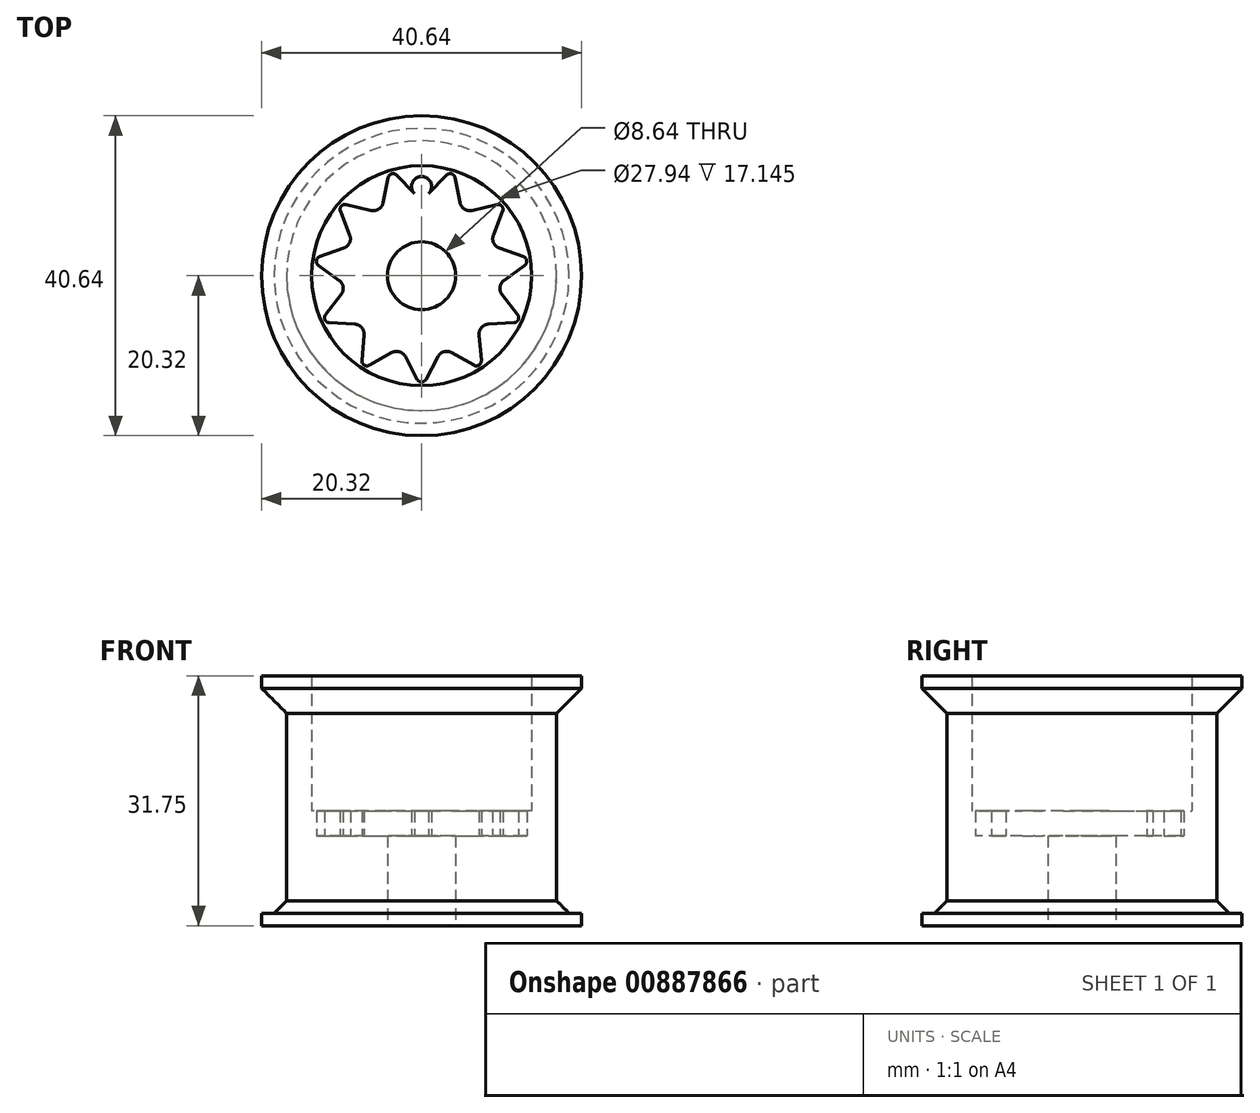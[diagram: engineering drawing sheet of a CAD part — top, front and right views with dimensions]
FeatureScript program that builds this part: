
annotation { "Feature Type Name" : "Feature", "Feature Type Description" : "" }
export const myFeature = defineFeature(function(context is Context, id is Id, definition is map)
    precondition{}
    {
        {
            var Q0;
            Q0=qCreatedBy(makeId("Top.planeOp"),FACE);
            var sketch = newSketch(context, id + "F0", { "sketchPlane" : qUnion([Q0])});
            skCircle(sketch, "E0", {"center": v(0, 0) * mm, "radius": 4.32 * mm});
            skCircle(sketch, "E1", {"center": v(0, 0) * mm, "radius": 15.88 * mm});
            skSolve(sketch);
        }
        {
            var Q0;
            Q0=makeQuery(id+"F0.imprint","IMPRINT",FACE,{"disambiguationData":[TD([[makeQuery(id+"F0.imprint","IMPRINT",EDGE,{"derivedFrom":sQuery(id+"F0.wireOp",EDGE,"E0")}),-1.0]])]});
            extrude(context, id + "F1", {"entities" : qUnion([Q0]), "depth" : 11.43 * mm, "offsetDistance" : 25.4 * mm});
        }
        {
            var Q0;
            Q0=qCreatedBy(makeId("Front.planeOp"),FACE);
            var sketch = newSketch(context, id + "F2", { "sketchPlane" : qUnion([Q0])});
            skLineSegment(sketch, "E2.bottom", {"start": v(0, 0) * mm, "end": v(-20.32, 0) * mm});
            skLineSegment(sketch, "E2.top", {"start": v(0, 0) * mm, "end": v(-20.32, 0) * mm});
            skLineSegment(sketch, "E2.left", {"start": v(0, 0) * mm, "end": v(0, 0) * mm});
            skLineSegment(sketch, "E2.right", {"start": v(-20.32, 0) * mm, "end": v(-20.32, 0) * mm});
            skLineSegment(sketch, "E3.top", {"start": v(-20.32, 1.59) * mm, "end": v(-20.32, 1.59) * mm});
            skLineSegment(sketch, "E3.left", {"start": v(-20.32, 0) * mm, "end": v(-20.32, 1.59) * mm});
            skLineSegment(sketch, "E3.right", {"start": v(-20.32, 0) * mm, "end": v(-20.32, 1.59) * mm});
            skLineSegment(sketch, "E4", {"start": v(-20.32, 1.59) * mm, "end": v(-17.15, 1.59) * mm});
            skLineSegment(sketch, "E5", {"start": v(-17.15, 1.59) * mm, "end": v(-17.15, 30.16) * mm});
            skLineSegment(sketch, "E6", {"start": v(-17.15, 30.16) * mm, "end": v(-20.32, 30.16) * mm});
            skLineSegment(sketch, "E7", {"start": v(-20.32, 30.16) * mm, "end": v(-20.32, 31.75) * mm});
            skLineSegment(sketch, "E8", {"start": v(-20.32, 31.75) * mm, "end": v(-13.97, 31.75) * mm});
            skLineSegment(sketch, "E9", {"start": v(0, 0) * mm, "end": v(-10.16, 0) * mm});
            skLineSegment(sketch, "E10", {"start": v(-10.16, 0) * mm, "end": v(-10.16, 1.59) * mm});
            skLineSegment(sketch, "E11", {"start": v(-10.16, 1.59) * mm, "end": v(-13.97, 1.59) * mm});
            skLineSegment(sketch, "E12", {"start": v(-13.97, 31.75) * mm, "end": v(-13.97, 1.59) * mm});
            skLineSegment(sketch, "E13", {"start": v(-20.32, 30.16) * mm, "end": v(-17.15, 26.99) * mm});
            skLineSegment(sketch, "E14", {"start": v(0, 0) * mm, "end": v(0, 23.16) * mm});
            skSolve(sketch);
        }
        {
            var Q0;
            {var subQ5=sQuery(id+"F2.wireOp",EDGE,"E3.left");Q0=makeQuery(id+"F2.imprint","IMPRINT",FACE,{"disambiguationData":[TD([[makeQuery(id+"F2.imprint","IMPRINT",EDGE,{"derivedFrom":subQ5}),-1.0]])]});}
            var Q1;
            {var subQ0=sQuery(id+"F2.wireOp",EDGE,"E6");Q1=makeQuery(id+"F2.imprint","IMPRINT",FACE,{"disambiguationData":[TD([[makeQuery(id+"F2.imprint","IMPRINT",EDGE,{"derivedFrom":subQ0}),1.0]])]});}
            var Q2;
            Q2=sQuery(id+"F2.wireOp",EDGE,"E14");
            revolve(context, id + "F3", {"operationType" : NewBodyOperationType.ADD, "surfaceOperationType" : NewSurfaceOperationType.NEW, "entities" : qUnion([Q0, Q1]), "axis" : qUnion([Q2]), "revolveType" : RevolveType.FULL});
        }
        {
            var Q0;
            Q0=makeQuery(id+"F1.opExtrude","CAP_FACE",FACE,{"disambiguationData":[OSD([sQuery(id+"F0.wireOp",EDGE,"E0"),sQuery(id+"F0.wireOp",EDGE,"E1")])],"isStart":false});
            var sketch = newSketch(context, id + "F4", { "sketchPlane" : qUnion([Q0])});
            skCircle(sketch, "E15", {"center": v(0, 0) * mm, "radius": 13.5 * mm});
            skLineSegment(sketch, "E16", {"start": v(0, 13.5) * mm, "end": v(0, 10.06) * mm});
            skCircle(sketch, "E17", {"center": v(0, 11.33) * mm, "radius": 1.27 * mm});
            skCircle(sketch, "E18.1.0", {"center": v(-6.13, 9.54) * mm, "radius": 1.27 * mm});
            skCircle(sketch, "E18.2.0", {"center": v(-10.31, 4.7) * mm, "radius": 1.27 * mm});
            skCircle(sketch, "E18.3.0", {"center": v(-11.22, -1.61) * mm, "radius": 1.27 * mm});
            skCircle(sketch, "E18.4.0", {"center": v(-8.57, -7.42) * mm, "radius": 1.27 * mm});
            skCircle(sketch, "E18.5.0", {"center": v(-3.2, -10.88) * mm, "radius": 1.27 * mm});
            skCircle(sketch, "E18.6.0", {"center": v(3.2, -10.88) * mm, "radius": 1.27 * mm});
            skCircle(sketch, "E18.7.0", {"center": v(8.57, -7.42) * mm, "radius": 1.27 * mm});
            skCircle(sketch, "E18.8.0", {"center": v(11.22, -1.61) * mm, "radius": 1.27 * mm});
            skCircle(sketch, "E18.9.0", {"center": v(10.31, 4.7) * mm, "radius": 1.27 * mm});
            skCircle(sketch, "E18.10.0", {"center": v(6.13, 9.54) * mm, "radius": 1.27 * mm});
            skLineSegment(sketch, "E19", {"start": v(0, 0) * mm, "end": v(3.8, 12.95) * mm});
            skCircle(sketch, "E20", {"center": v(3.62, 12.34) * mm, "radius": 0.64 * mm});
            skCircle(sketch, "E21.1.0", {"center": v(-3.62, 12.34) * mm, "radius": 0.64 * mm});
            skCircle(sketch, "E21.2.0", {"center": v(-9.72, 8.42) * mm, "radius": 0.64 * mm});
            skCircle(sketch, "E22.1.3.0", {"center": v(-12.73, 1.83) * mm, "radius": 0.64 * mm});
            skCircle(sketch, "E22.1.4.0", {"center": v(-11.7, -5.34) * mm, "radius": 0.64 * mm});
            skCircle(sketch, "E22.1.5.0", {"center": v(-6.95, -10.82) * mm, "radius": 0.64 * mm});
            skCircle(sketch, "E22.1.6.0", {"center": v(0, -12.86) * mm, "radius": 0.64 * mm});
            skCircle(sketch, "E22.1.7.0", {"center": v(6.95, -10.82) * mm, "radius": 0.64 * mm});
            skCircle(sketch, "E22.1.8.0", {"center": v(11.7, -5.34) * mm, "radius": 0.64 * mm});
            skCircle(sketch, "E22.1.9.0", {"center": v(12.73, 1.83) * mm, "radius": 0.64 * mm});
            skCircle(sketch, "E22.1.10.0", {"center": v(9.72, 8.42) * mm, "radius": 0.64 * mm});
            skLineSegment(sketch, "E23", {"start": v(-9.13, 5.17) * mm, "end": v(-10.3, 8.19) * mm});
            skLineSegment(sketch, "E24", {"start": v(-9.89, 3.51) * mm, "end": v(-12.94, 2.43) * mm});
            skLineSegment(sketch, "E25", {"start": v(-9.57, 9.04) * mm, "end": v(-6.42, 8.3) * mm});
            skLineSegment(sketch, "E26", {"start": v(-13.1, 1.32) * mm, "end": v(-10.47, -0.58) * mm});
            skLineSegment(sketch, "E27", {"start": v(-10.22, -2.4) * mm, "end": v(-12.2, -4.95) * mm});
            skLineSegment(sketch, "E28", {"start": v(-7.3, -7.53) * mm, "end": v(-7.58, -10.76) * mm});
            skLineSegment(sketch, "E29", {"start": v(-6.64, -11.37) * mm, "end": v(-3.82, -9.77) * mm});
            skLineSegment(sketch, "E30", {"start": v(-2.07, -10.29) * mm, "end": v(-0.56, -13.15) * mm});
            skLineSegment(sketch, "E31", {"start": v(0.56, -13.15) * mm, "end": v(2.07, -10.29) * mm});
            skLineSegment(sketch, "E32", {"start": v(3.82, -9.77) * mm, "end": v(6.64, -11.37) * mm});
            skLineSegment(sketch, "E33", {"start": v(7.58, -10.76) * mm, "end": v(7.3, -7.53) * mm});
            skLineSegment(sketch, "E34", {"start": v(8.5, -6.15) * mm, "end": v(11.73, -5.98) * mm});
            skLineSegment(sketch, "E35", {"start": v(-4.88, 9.29) * mm, "end": v(-4.25, 12.46) * mm});
            skLineSegment(sketch, "E36", {"start": v(-3.17, 12.78) * mm, "end": v(-0.91, 10.45) * mm});
            skLineSegment(sketch, "E37", {"start": v(0.91, 10.45) * mm, "end": v(3.17, 12.78) * mm});
            skLineSegment(sketch, "E38", {"start": v(10.3, 8.19) * mm, "end": v(9.13, 5.17) * mm});
            skLineSegment(sketch, "E39", {"start": v(9.89, 3.51) * mm, "end": v(12.94, 2.43) * mm});
            skLineSegment(sketch, "E40", {"start": v(13.1, 1.32) * mm, "end": v(10.47, -0.58) * mm});
            skLineSegment(sketch, "E41", {"start": v(10.22, -2.4) * mm, "end": v(12.2, -4.95) * mm});
            skLineSegment(sketch, "E42", {"start": v(4.25, 12.46) * mm, "end": v(4.88, 9.29) * mm});
            skLineSegment(sketch, "E43", {"start": v(6.42, 8.3) * mm, "end": v(9.57, 9.04) * mm});
            skLineSegment(sketch, "E44", {"start": v(-11.73, -5.98) * mm, "end": v(-8.5, -6.15) * mm});
            skCircle(sketch, "E45", {"center": v(0, 0) * mm, "radius": 15.88 * mm});
            skSolve(sketch);
        }
        {
            var Q0;
            Q0=makeQuery(id+"F3.opRevolve","SWEPT_EDGE",EDGE,{"disambiguationData":[OSD([sQuery(id+"F2.wireOp",EDGE,"E4"),sQuery(id+"F2.wireOp",EDGE,"E5")])]});
            chamfer(context, id + "F5", {"entities" : qUnion([Q0]), "width" : 1.59 * mm, "tangentPropagation" : true});
        }
        {
            var Q0;
            Q0=makeQuery(id+"F4.imprint","IMPRINT",FACE,{"disambiguationData":[TD([[makeQuery(id+"F4.imprint","IMPRINT",EDGE,{"derivedFrom":makeQuery(id+"F3.boolean.opBoolean","INTERSECT",EDGE,{"derivedFrom":[makeQuery(id+"F1.opExtrude","CAP_FACE",FACE,{"disambiguationData":[OSD([sQuery(id+"F0.wireOp",EDGE,"E0"),sQuery(id+"F0.wireOp",EDGE,"E1")])],"isStart":false}),makeQuery(id+"F3.opRevolve","SWEPT_FACE",FACE,{"disambiguationData":[OSD([sQuery(id+"F2.wireOp",EDGE,"E12")])]})]})}),-1.0]])]});
            var Q1;
            {var subQ4=sQuery(id+"F4.wireOp",EDGE,"E38");Q1=makeQuery(id+"F4.imprint","IMPRINT",FACE,{"disambiguationData":[TD([[makeQuery(id+"F4.imprint","IMPRINT",EDGE,{"derivedFrom":subQ4}),1.0]])]});}
            var Q2;
            {var subQ0=sQuery(id+"F4.wireOp",EDGE,"E18.9.0");var subQ1=makeQuery(id+"F4.imprint","INTERSECT",VERTEX,{"derivedFrom":[subQ0,sQuery(id+"F4.wireOp",EDGE,"E38")]});Q2=makeQuery(id+"F4.imprint","IMPRINT",FACE,{"disambiguationData":[TD([[makeQuery(id+"F4.imprint","IMPRINT",EDGE,{"disambiguationData":[TD([[subQ1,-1.0]])],"derivedFrom":subQ0}),1.0]])]});}
            var Q3;
            {var subQ0=sQuery(id+"F4.wireOp",EDGE,"E40");Q3=makeQuery(id+"F4.imprint","IMPRINT",FACE,{"disambiguationData":[TD([[makeQuery(id+"F4.imprint","IMPRINT",EDGE,{"derivedFrom":subQ0}),1.0]])]});}
            var Q4;
            {var subQ0=sQuery(id+"F4.wireOp",EDGE,"E18.8.0");var subQ1=makeQuery(id+"F4.imprint","INTERSECT",VERTEX,{"derivedFrom":[subQ0,sQuery(id+"F4.wireOp",EDGE,"E40")]});Q4=makeQuery(id+"F4.imprint","IMPRINT",FACE,{"disambiguationData":[TD([[makeQuery(id+"F4.imprint","IMPRINT",EDGE,{"disambiguationData":[TD([[subQ1,-1.0]])],"derivedFrom":subQ0}),1.0]])]});}
            var Q5;
            {var subQ4=sQuery(id+"F4.wireOp",EDGE,"E33");Q5=makeQuery(id+"F4.imprint","IMPRINT",FACE,{"disambiguationData":[TD([[makeQuery(id+"F4.imprint","IMPRINT",EDGE,{"derivedFrom":subQ4}),-1.0]])]});}
            var Q6;
            {var subQ0=sQuery(id+"F4.wireOp",EDGE,"E18.7.0");var subQ1=makeQuery(id+"F4.imprint","INTERSECT",VERTEX,{"derivedFrom":[subQ0,sQuery(id+"F4.wireOp",EDGE,"E33")]});Q6=makeQuery(id+"F4.imprint","IMPRINT",FACE,{"disambiguationData":[TD([[makeQuery(id+"F4.imprint","IMPRINT",EDGE,{"disambiguationData":[TD([[subQ1,1.0]])],"derivedFrom":subQ0}),1.0]])]});}
            var Q7;
            {var subQ4=sQuery(id+"F4.wireOp",EDGE,"E31");Q7=makeQuery(id+"F4.imprint","IMPRINT",FACE,{"disambiguationData":[TD([[makeQuery(id+"F4.imprint","IMPRINT",EDGE,{"derivedFrom":subQ4}),-1.0]])]});}
            var Q8;
            {var subQ0=sQuery(id+"F4.wireOp",EDGE,"E18.6.0");var subQ1=makeQuery(id+"F4.imprint","INTERSECT",VERTEX,{"derivedFrom":[subQ0,sQuery(id+"F4.wireOp",EDGE,"E31")]});Q8=makeQuery(id+"F4.imprint","IMPRINT",FACE,{"disambiguationData":[TD([[makeQuery(id+"F4.imprint","IMPRINT",EDGE,{"disambiguationData":[TD([[subQ1,1.0]])],"derivedFrom":subQ0}),1.0]])]});}
            var Q9;
            {var subQ0=sQuery(id+"F4.wireOp",EDGE,"E29");Q9=makeQuery(id+"F4.imprint","IMPRINT",FACE,{"disambiguationData":[TD([[makeQuery(id+"F4.imprint","IMPRINT",EDGE,{"derivedFrom":subQ0}),-1.0]])]});}
            var Q10;
            {var subQ0=sQuery(id+"F4.wireOp",EDGE,"E18.5.0");var subQ1=makeQuery(id+"F4.imprint","INTERSECT",VERTEX,{"derivedFrom":[subQ0,sQuery(id+"F4.wireOp",EDGE,"E29")]});Q10=makeQuery(id+"F4.imprint","IMPRINT",FACE,{"disambiguationData":[TD([[makeQuery(id+"F4.imprint","IMPRINT",EDGE,{"disambiguationData":[TD([[subQ1,1.0]])],"derivedFrom":subQ0}),1.0]])]});}
            var Q11;
            {var subQ4=sQuery(id+"F4.wireOp",EDGE,"E28");Q11=makeQuery(id+"F4.imprint","IMPRINT",FACE,{"disambiguationData":[TD([[makeQuery(id+"F4.imprint","IMPRINT",EDGE,{"derivedFrom":subQ4}),-1.0]])]});}
            var Q12;
            {var subQ0=sQuery(id+"F4.wireOp",EDGE,"E18.4.0");var subQ1=makeQuery(id+"F4.imprint","INTERSECT",VERTEX,{"derivedFrom":[subQ0,sQuery(id+"F4.wireOp",EDGE,"E28")]});Q12=makeQuery(id+"F4.imprint","IMPRINT",FACE,{"disambiguationData":[TD([[makeQuery(id+"F4.imprint","IMPRINT",EDGE,{"disambiguationData":[TD([[subQ1,-1.0]])],"derivedFrom":subQ0}),1.0]])]});}
            var Q13;
            {var subQ4=sQuery(id+"F4.wireOp",EDGE,"E26");Q13=makeQuery(id+"F4.imprint","IMPRINT",FACE,{"disambiguationData":[TD([[makeQuery(id+"F4.imprint","IMPRINT",EDGE,{"derivedFrom":subQ4}),-1.0]])]});}
            var Q14;
            {var subQ0=sQuery(id+"F4.wireOp",EDGE,"E18.3.0");var subQ1=makeQuery(id+"F4.imprint","INTERSECT",VERTEX,{"derivedFrom":[subQ0,sQuery(id+"F4.wireOp",EDGE,"E26")]});Q14=makeQuery(id+"F4.imprint","IMPRINT",FACE,{"disambiguationData":[TD([[makeQuery(id+"F4.imprint","IMPRINT",EDGE,{"disambiguationData":[TD([[subQ1,1.0]])],"derivedFrom":subQ0}),1.0]])]});}
            var Q15;
            {var subQ6=sQuery(id+"F4.wireOp",EDGE,"E23");Q15=makeQuery(id+"F4.imprint","IMPRINT",FACE,{"disambiguationData":[TD([[makeQuery(id+"F4.imprint","IMPRINT",EDGE,{"derivedFrom":subQ6}),1.0]])]});}
            var Q16;
            {var subQ0=sQuery(id+"F4.wireOp",EDGE,"E18.2.0");var subQ1=makeQuery(id+"F4.imprint","INTERSECT",VERTEX,{"derivedFrom":[subQ0,sQuery(id+"F4.wireOp",EDGE,"E23")]});Q16=makeQuery(id+"F4.imprint","IMPRINT",FACE,{"disambiguationData":[TD([[makeQuery(id+"F4.imprint","IMPRINT",EDGE,{"disambiguationData":[TD([[subQ1,1.0]])],"derivedFrom":subQ0}),1.0]])]});}
            var Q17;
            {var subQ0=sQuery(id+"F4.wireOp",EDGE,"E25");Q17=makeQuery(id+"F4.imprint","IMPRINT",FACE,{"disambiguationData":[TD([[makeQuery(id+"F4.imprint","IMPRINT",EDGE,{"derivedFrom":subQ0}),1.0]])]});}
            var Q18;
            {var subQ0=sQuery(id+"F4.wireOp",EDGE,"E18.1.0");var subQ1=makeQuery(id+"F4.imprint","INTERSECT",VERTEX,{"derivedFrom":[subQ0,sQuery(id+"F4.wireOp",EDGE,"E25")]});Q18=makeQuery(id+"F4.imprint","IMPRINT",FACE,{"disambiguationData":[TD([[makeQuery(id+"F4.imprint","IMPRINT",EDGE,{"disambiguationData":[TD([[subQ1,-1.0]])],"derivedFrom":subQ0}),1.0]])]});}
            var Q19;
            {var subQ0=sQuery(id+"F4.wireOp",EDGE,"E36");Q19=makeQuery(id+"F4.imprint","IMPRINT",FACE,{"disambiguationData":[TD([[makeQuery(id+"F4.imprint","IMPRINT",EDGE,{"derivedFrom":subQ0}),1.0]])]});}
            var Q20;
            {var subQ0=sQuery(id+"F4.wireOp",EDGE,"E17");var subQ1=sQuery(id+"F4.wireOp",EDGE,"E16");var subQ2=makeQuery(id+"F4.imprint","INTERSECT",VERTEX,{"disambiguationData":[OD(0.0)],"derivedFrom":[subQ1,subQ0]});Q20=makeQuery(id+"F4.imprint","IMPRINT",FACE,{"disambiguationData":[TD([[makeQuery(id+"F4.imprint","IMPRINT",EDGE,{"disambiguationData":[TD([[subQ2,1.0]])],"derivedFrom":subQ1}),-1.0]])]});}
            var Q21;
            {var subQ0=sQuery(id+"F4.wireOp",EDGE,"E17");var subQ1=sQuery(id+"F4.wireOp",EDGE,"E16");var subQ2=makeQuery(id+"F4.imprint","INTERSECT",VERTEX,{"disambiguationData":[OD(0.0)],"derivedFrom":[subQ1,subQ0]});Q21=makeQuery(id+"F4.imprint","IMPRINT",FACE,{"disambiguationData":[TD([[makeQuery(id+"F4.imprint","IMPRINT",EDGE,{"disambiguationData":[TD([[subQ2,1.0]])],"derivedFrom":subQ1}),1.0]])]});}
            var Q22;
            {var subQ3=sQuery(id+"F4.wireOp",EDGE,"E37");Q22=makeQuery(id+"F4.imprint","IMPRINT",FACE,{"disambiguationData":[TD([[makeQuery(id+"F4.imprint","IMPRINT",EDGE,{"derivedFrom":subQ3}),1.0]])]});}
            var Q23;
            {var subQ3=sQuery(id+"F4.wireOp",EDGE,"E42");Q23=makeQuery(id+"F4.imprint","IMPRINT",FACE,{"disambiguationData":[TD([[makeQuery(id+"F4.imprint","IMPRINT",EDGE,{"derivedFrom":subQ3}),1.0]])]});}
            var Q24;
            {var subQ0=sQuery(id+"F4.wireOp",EDGE,"E18.10.0");var subQ1=makeQuery(id+"F4.imprint","INTERSECT",VERTEX,{"derivedFrom":[subQ0,sQuery(id+"F4.wireOp",EDGE,"E42")]});Q24=makeQuery(id+"F4.imprint","IMPRINT",FACE,{"disambiguationData":[TD([[makeQuery(id+"F4.imprint","IMPRINT",EDGE,{"disambiguationData":[TD([[subQ1,-1.0]])],"derivedFrom":subQ0}),1.0]])]});}
            extrude(context, id + "F6", {"entities" : qUnion([Q0, Q1, Q2, Q3, Q4, Q5, Q6, Q7, Q8, Q9, Q10, Q11, Q12, Q13, Q14, Q15, Q16, Q17, Q18, Q19, Q20, Q21, Q22, Q23, Q24]), "operationType" : NewBodyOperationType.ADD, "depth" : 3.17 * mm, "offsetDistance" : 25.4 * mm});
        }
    });
